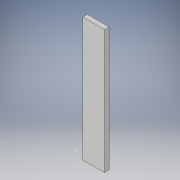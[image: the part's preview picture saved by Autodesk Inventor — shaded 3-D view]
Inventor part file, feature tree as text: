
AUTODESK INVENTOR PART (.ipt)
format: ipt  version: 2017 (Build 210142000, 142)  size: 130,560 bytes
history: native  units: in
note: dims shown in document units (in); Inventor stores cm internally (conversion verified against a paired STEP export)
features: sketch x4, extrude x2, hole x1
ambient origin geometry x8: Origin, YZ Plane, XZ Plane, XY Plane, X Axis, Y Axis, Z Axis, Center Point
bodies: Solid1 (feature_tree)
feature tree (7):
  extrude  "Extrusion1"  Depth=10.0in
  extrude  "Extrusion4"  Depth=0.375in
  sketch  "Sketch5"  dims[d12=5.0in d13=0.0in]
  hole  "Hole2"  [1 undecoded]
  sketch  "Sketch1"  dims[d0=2.725in d1=10.0in]
  sketch  "Sketch4"  dims[d2=0.375in d3=0.0in d11=0.975in]
  sketch  "Sketch9"  dims[d34=0.13in d35=0.25in d36=0.375in d37=0.25in d38=0.5635in d39=0.3in d40=0.8108in]
note: 1 required parameter value undecoded (feature->parameter linkage not recoverable at this tier; creation-order binding heuristic only, values carry confidence <= 0.55)
